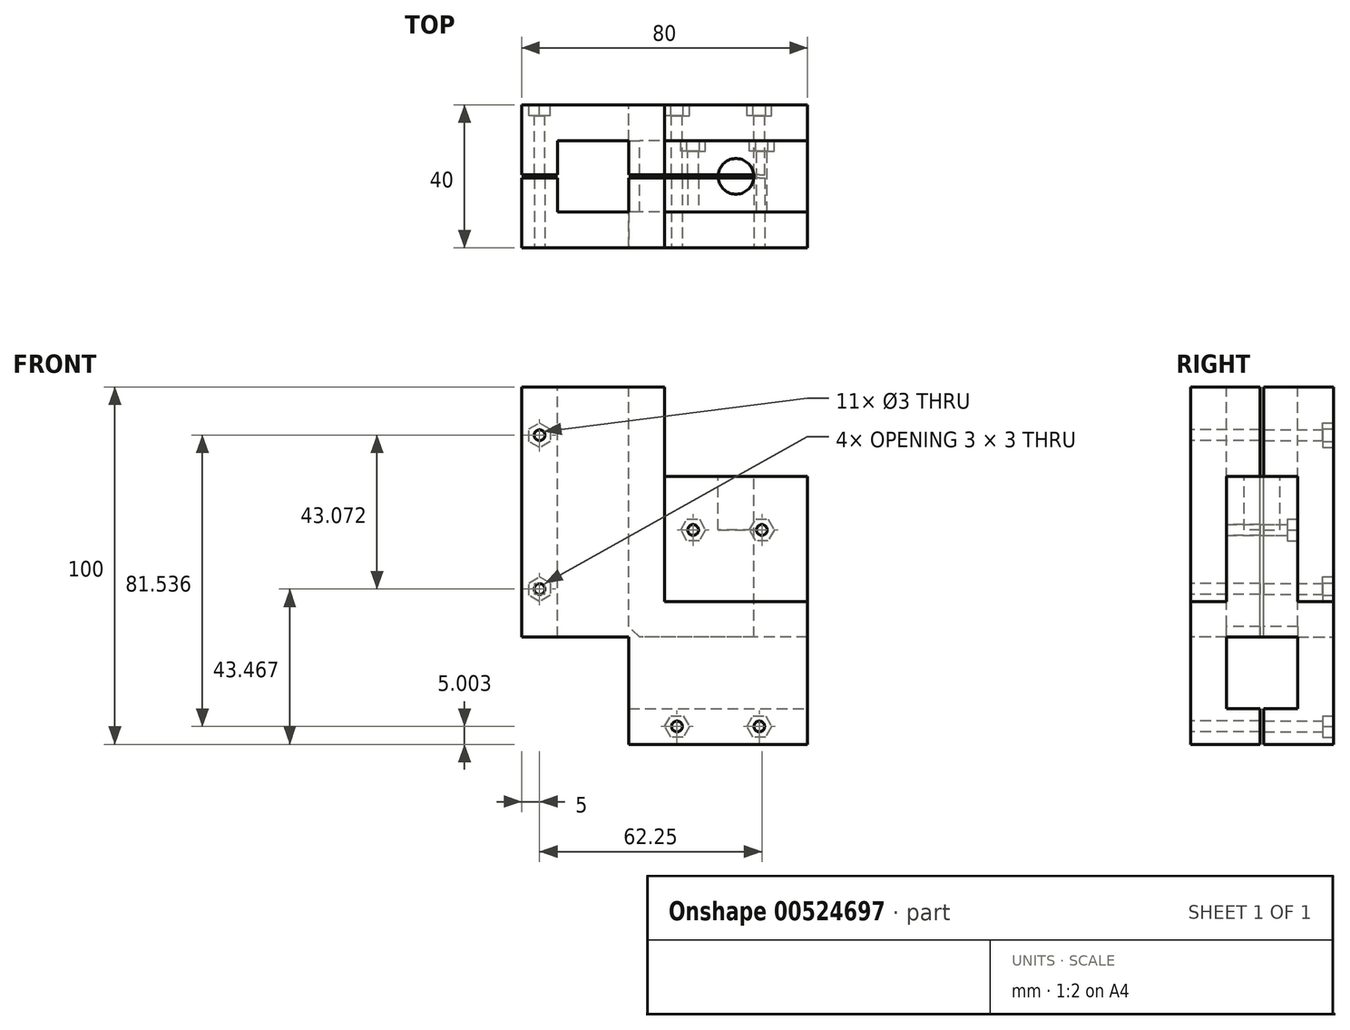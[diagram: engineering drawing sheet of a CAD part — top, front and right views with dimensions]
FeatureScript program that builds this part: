
annotation { "Feature Type Name" : "Feature", "Feature Type Description" : "" }
export const myFeature = defineFeature(function(context is Context, id is Id, definition is map)
    precondition{}
    {
        {
            var Q0;
            Q0=qCreatedBy(makeId("Front.planeOp"),FACE);
            var sketch = newSketch(context, id + "F0", { "sketchPlane" : qUnion([Q0])});
            skLineSegment(sketch, "E0", {"start": v(-50, 89.2) * mm, "end": v(-50, 19.2) * mm});
            skLineSegment(sketch, "E1", {"start": v(-50, 19.2) * mm, "end": v(0, 19.2) * mm});
            skLineSegment(sketch, "E2", {"start": v(0, 19.2) * mm, "end": v(0, 64.2) * mm});
            skLineSegment(sketch, "E3", {"start": v(0, 64.2) * mm, "end": v(-40, 64.2) * mm});
            skLineSegment(sketch, "E4", {"start": v(-40, 64.2) * mm, "end": v(-40, 89.2) * mm});
            skLineSegment(sketch, "E5", {"start": v(-40, 89.2) * mm, "end": v(-50, 89.2) * mm});
            skSolve(sketch);
        }
        {
            var Q0;
            Q0=qSketchRegion(id+"F0",true);
            extrude(context, id + "F1", {"entities" : qUnion([Q0]), "depth" : 20 * mm, "offsetDistance" : 25 * mm});
        }
        {
            var Q0;
            Q0=makeQuery(id+"F1.opExtrude","CAP_FACE",FACE,{"disambiguationData":[OSD([sQuery(id+"F0.wireOp",EDGE,"E0"),sQuery(id+"F0.wireOp",EDGE,"E1"),sQuery(id+"F0.wireOp",EDGE,"E2"),sQuery(id+"F0.wireOp",EDGE,"E3"),sQuery(id+"F0.wireOp",EDGE,"E4"),sQuery(id+"F0.wireOp",EDGE,"E5")])],"isStart":false});
            var sketch = newSketch(context, id + "F2", { "sketchPlane" : qUnion([Q0])});
            skLineSegment(sketch, "E6", {"start": v(-50, 29.2) * mm, "end": v(0, 29.2) * mm});
            skSolve(sketch);
        }
        {
            var Q0;
            {var subQ0=sQuery(id+"F2.wireOp",EDGE,"E6");Q0=makeQuery(id+"F2.imprint","IMPRINT",FACE,{"disambiguationData":[TD([[makeQuery(id+"F2.imprint","IMPRINT",EDGE,{"derivedFrom":subQ0}),-1.0]])]});}
            extrude(context, id + "F3", {"entities" : qUnion([Q0]), "operationType" : NewBodyOperationType.ADD, "depth" : 10 * mm, "offsetDistance" : 25 * mm});
        }
        {
            var Q0;
            Q0=makeQuery(id+"F1.opExtrude","CAP_FACE",FACE,{"disambiguationData":[OSD([sQuery(id+"F0.wireOp",EDGE,"E0"),sQuery(id+"F0.wireOp",EDGE,"E1"),sQuery(id+"F0.wireOp",EDGE,"E2"),sQuery(id+"F0.wireOp",EDGE,"E3"),sQuery(id+"F0.wireOp",EDGE,"E4"),sQuery(id+"F0.wireOp",EDGE,"E5")])],"isStart":true});
            var sketch = newSketch(context, id + "F4", { "sketchPlane" : qUnion([Q0])});
            skLineSegment(sketch, "E7", {"start": v(0, 29.2) * mm, "end": v(50, 29.2) * mm});
            skSolve(sketch);
        }
        {
            var Q0;
            {var subQ0=sQuery(id+"F4.wireOp",EDGE,"E7");Q0=makeQuery(id+"F4.imprint","IMPRINT",FACE,{"disambiguationData":[TD([[makeQuery(id+"F4.imprint","IMPRINT",EDGE,{"derivedFrom":subQ0}),-1.0]])]});}
            extrude(context, id + "F5", {"entities" : qUnion([Q0]), "operationType" : NewBodyOperationType.ADD, "depth" : 10 * mm, "offsetDistance" : 25 * mm});
        }
        {
            var Q0;
            {var subQ0=sQuery(id+"F0.wireOp",EDGE,"E1");Q0=makeQuery(id+"F5.boolean.opBoolean","MERGE",FACE,{"derivedFrom":[makeQuery(id+"F3.boolean.opBoolean","MERGE",FACE,{"derivedFrom":[makeQuery(id+"F1.opExtrude","SWEPT_FACE",FACE,{"disambiguationData":[OSD([subQ0])]}),makeQuery(id+"F3.opExtrude","SWEPT_FACE",FACE,{"disambiguationData":[OSD([subQ0])]})]}),makeQuery(id+"F5.opExtrude","SWEPT_FACE",FACE,{"disambiguationData":[OSD([subQ0])]})]});}
            var sketch = newSketch(context, id + "F6", { "sketchPlane" : qUnion([Q0])});
            skLineSegment(sketch, "E8", {"start": v(0, 20) * mm, "end": v(-50, 20) * mm});
            skLineSegment(sketch, "E9", {"start": v(0, 0) * mm, "end": v(-50, 0) * mm});
            skSolve(sketch);
        }
        {
            var Q0;
            {var subQ0=sQuery(id+"F6.wireOp",EDGE,"E8");Q0=makeQuery(id+"F6.imprint","IMPRINT",FACE,{"disambiguationData":[TD([[makeQuery(id+"F6.imprint","IMPRINT",EDGE,{"derivedFrom":subQ0}),-1.0]])]});}
            var Q1;
            {var subQ0=sQuery(id+"F6.wireOp",EDGE,"E9");Q1=makeQuery(id+"F6.imprint","IMPRINT",FACE,{"disambiguationData":[TD([[makeQuery(id+"F6.imprint","IMPRINT",EDGE,{"derivedFrom":subQ0}),1.0]])]});}
            extrude(context, id + "F7", {"entities" : qUnion([Q0, Q1]), "operationType" : NewBodyOperationType.ADD, "depth" : 30 * mm, "offsetDistance" : 25 * mm});
        }
        {
            var Q0;
            Q0=makeQuery(id+"F5.opExtrude","SWEPT_FACE",FACE,{"disambiguationData":[OSD([sQuery(id+"F4.wireOp",EDGE,"E7")])]});
            var sketch = newSketch(context, id + "F8", { "sketchPlane" : qUnion([Q0])});
            skLineSegment(sketch, "E10", {"start": v(-30, -25) * mm, "end": v(-28.27, -28) * mm});
            skLineSegment(sketch, "E11", {"start": v(-28.27, -28) * mm, "end": v(-24.8, -28) * mm});
            skLineSegment(sketch, "E12", {"start": v(-24.8, -28) * mm, "end": v(-23.07, -25) * mm});
            skLineSegment(sketch, "E13", {"start": v(-23.07, -25) * mm, "end": v(-24.8, -22) * mm});
            skLineSegment(sketch, "E14", {"start": v(-24.8, -22) * mm, "end": v(-28.27, -22) * mm});
            skLineSegment(sketch, "E15", {"start": v(-28.27, -22) * mm, "end": v(-30, -25) * mm});
            skCircle(sketch, "E16", {"center": v(-26.54, -25) * mm, "radius": 1.5 * mm});
            skLineSegment(sketch, "E17", {"start": v(-16.93, -25) * mm, "end": v(-15.2, -28) * mm});
            skLineSegment(sketch, "E18", {"start": v(-15.2, -28) * mm, "end": v(-11.73, -28) * mm});
            skLineSegment(sketch, "E19", {"start": v(-11.73, -28) * mm, "end": v(-10, -25) * mm});
            skLineSegment(sketch, "E20", {"start": v(-10, -25) * mm, "end": v(-11.73, -22) * mm});
            skLineSegment(sketch, "E21", {"start": v(-11.73, -22) * mm, "end": v(-15.2, -22) * mm});
            skLineSegment(sketch, "E22", {"start": v(-15.2, -22) * mm, "end": v(-16.93, -25) * mm});
            skCircle(sketch, "E23", {"center": v(-13.46, -25) * mm, "radius": 1.5 * mm});
            skLineSegment(sketch, "E24", {"start": v(-70, 5) * mm, "end": v(-68.27, 2) * mm});
            skLineSegment(sketch, "E25", {"start": v(-68.27, 2) * mm, "end": v(-64.8, 2) * mm});
            skLineSegment(sketch, "E26", {"start": v(-64.8, 2) * mm, "end": v(-63.07, 5) * mm});
            skLineSegment(sketch, "E27", {"start": v(-63.07, 5) * mm, "end": v(-64.8, 8) * mm});
            skLineSegment(sketch, "E28", {"start": v(-64.8, 8) * mm, "end": v(-68.27, 8) * mm});
            skLineSegment(sketch, "E29", {"start": v(-68.27, 8) * mm, "end": v(-70, 5) * mm});
            skCircle(sketch, "E30", {"center": v(-66.54, 5) * mm, "radius": 1.5 * mm});
            skLineSegment(sketch, "E31", {"start": v(-16.93, 5) * mm, "end": v(-15.2, 2) * mm});
            skLineSegment(sketch, "E32", {"start": v(-15.2, 2) * mm, "end": v(-11.73, 2) * mm});
            skLineSegment(sketch, "E33", {"start": v(-11.73, 2) * mm, "end": v(-10, 5) * mm});
            skLineSegment(sketch, "E34", {"start": v(-10, 5) * mm, "end": v(-11.73, 8) * mm});
            skLineSegment(sketch, "E35", {"start": v(-11.73, 8) * mm, "end": v(-15.2, 8) * mm});
            skLineSegment(sketch, "E36", {"start": v(-15.2, 8) * mm, "end": v(-16.93, 5) * mm});
            skCircle(sketch, "E37", {"center": v(-13.46, 5) * mm, "radius": 1.5 * mm});
            skLineSegment(sketch, "E38", {"start": v(-40, 0) * mm, "end": v(-40, 10) * mm});
            skLineSegment(sketch, "E39.bottom", {"start": v(-40, -20) * mm, "end": v(-50, -20) * mm});
            skLineSegment(sketch, "E39.top", {"start": v(-40, -30) * mm, "end": v(-50, -30) * mm});
            skLineSegment(sketch, "E39.left", {"start": v(-40, -20) * mm, "end": v(-40, -30) * mm});
            skLineSegment(sketch, "E39.right", {"start": v(-50, -20) * mm, "end": v(-50, -30) * mm});
            skSolve(sketch);
        }
        {
            var Q0;
            {var subQ0=sQuery(id+"F8.wireOp",EDGE,"E38");Q0=makeQuery(id+"F8.imprint","IMPRINT",FACE,{"disambiguationData":[TD([[makeQuery(id+"F8.imprint","IMPRINT",EDGE,{"derivedFrom":subQ0}),1.0]])]});}
            var Q1;
            Q1=makeQuery(id+"F8.imprint","IMPRINT",FACE,{"disambiguationData":[TD([[makeQuery(id+"F8.imprint","IMPRINT",EDGE,{"derivedFrom":sQuery(id+"F8.wireOp",EDGE,"E39.bottom")}),1.0]])]});
            extrude(context, id + "F9", {"entities" : qUnion([Q0, Q1]), "operationType" : NewBodyOperationType.ADD, "depth" : 60 * mm, "offsetDistance" : 25 * mm});
        }
        {
            var Q0;
            {var subQ0=sQuery(id+"F0.wireOp",EDGE,"E0");var subQ1=sQuery(id+"F0.wireOp",EDGE,"E1");var subQ2=makeQuery(id+"F5.boolean.opBoolean","MERGE",EDGE,{"derivedFrom":[makeQuery(id+"F3.boolean.opBoolean","MERGE",EDGE,{"derivedFrom":[makeQuery(id+"F1.opExtrude","SWEPT_EDGE",EDGE,{"disambiguationData":[OSD([subQ0,subQ1])]}),makeQuery(id+"F3.opExtrude","SWEPT_EDGE",EDGE,{"disambiguationData":[OSD([subQ0,subQ1])]})]}),makeQuery(id+"F5.opExtrude","SWEPT_EDGE",EDGE,{"disambiguationData":[OSD([subQ0,subQ1])]})]});Q0=makeQuery(id+"F9.boolean.opBoolean","MERGE",FACE,{"derivedFrom":[makeQuery(id+"F7.boolean.opBoolean","MERGE",FACE,{"derivedFrom":[makeQuery(id+"F5.boolean.opBoolean","MERGE",FACE,{"derivedFrom":[makeQuery(id+"F3.boolean.opBoolean","MERGE",FACE,{"derivedFrom":[makeQuery(id+"F1.opExtrude","SWEPT_FACE",FACE,{"disambiguationData":[OSD([subQ0])]}),makeQuery(id+"F3.opExtrude","SWEPT_FACE",FACE,{"disambiguationData":[OSD([subQ0])]})]}),makeQuery(id+"F5.opExtrude","SWEPT_FACE",FACE,{"disambiguationData":[OSD([subQ0])]})]}),makeQuery(id+"F7.opExtrude","SWEPT_FACE",FACE,{"disambiguationData":[OSD([subQ0,subQ1]),TDD([makeQuery(id+"F6.imprint","IMPRINT",EDGE,{"disambiguationData":[TD([[makeQuery(id+"F6.imprint","INTERSECT",VERTEX,{"derivedFrom":[makeQuery(id+"F3.opExtrude","CAP_EDGE",EDGE,{"disambiguationData":[OSD([subQ1])],"isStart":false}),subQ2]}),-1.0]])],"derivedFrom":subQ2})])]}),makeQuery(id+"F7.opExtrude","SWEPT_FACE",FACE,{"disambiguationData":[OSD([subQ0,subQ1]),TDD([makeQuery(id+"F6.imprint","IMPRINT",EDGE,{"disambiguationData":[TD([[makeQuery(id+"F6.imprint","INTERSECT",VERTEX,{"derivedFrom":[makeQuery(id+"F5.opExtrude","CAP_EDGE",EDGE,{"disambiguationData":[OSD([subQ1])],"isStart":false}),subQ2]}),1.0]])],"derivedFrom":subQ2})])]})]}),makeQuery(id+"F9.opExtrude","SWEPT_FACE",FACE,{"disambiguationData":[OSD([sQuery(id+"F8.wireOp",EDGE,"E39.right")])]}),makeQuery(id+"F9.opExtrude","SWEPT_FACE",FACE,{"disambiguationData":[OSD([subQ0,sQuery(id+"F4.wireOp",EDGE,"E7")])]})]});}
            var sketch = newSketch(context, id + "F10", { "sketchPlane" : qUnion([Q0])});
            skLineSegment(sketch, "E40", {"start": v(20, 19.2) * mm, "end": v(20, 89.2) * mm});
            skLineSegment(sketch, "E41", {"start": v(0, 19.2) * mm, "end": v(0, 89.2) * mm});
            skLineSegment(sketch, "E42", {"start": v(20, 19.2) * mm, "end": v(30, 19.2) * mm});
            skLineSegment(sketch, "E43", {"start": v(0, 19.2) * mm, "end": v(-10, 19.2) * mm});
            skSolve(sketch);
        }
        {
            var Q0;
            {var subQ0=sQuery(id+"F10.wireOp",EDGE,"E40");Q0=makeQuery(id+"F10.imprint","IMPRINT",FACE,{"disambiguationData":[TD([[makeQuery(id+"F10.imprint","IMPRINT",EDGE,{"derivedFrom":subQ0}),-1.0]])]});}
            var Q1;
            {var subQ0=sQuery(id+"F10.wireOp",EDGE,"E41");Q1=makeQuery(id+"F10.imprint","IMPRINT",FACE,{"disambiguationData":[TD([[makeQuery(id+"F10.imprint","IMPRINT",EDGE,{"derivedFrom":subQ0}),1.0]])]});}
            extrude(context, id + "F11", {"entities" : qUnion([Q0, Q1]), "operationType" : NewBodyOperationType.ADD, "depth" : 30 * mm, "offsetDistance" : 25 * mm});
        }
        {
            var Q0;
            Q0=makeQuery(id+"F1.opExtrude","SWEPT_FACE",FACE,{"disambiguationData":[OSD([sQuery(id+"F0.wireOp",EDGE,"E3")])]});
            var sketch = newSketch(context, id + "F12", { "sketchPlane" : qUnion([Q0])});
            skCircle(sketch, "E44", {"center": v(-20, -10) * mm, "radius": 5 * mm});
            skSolve(sketch);
        }
        {
            var Q0;
            Q0=makeQuery(id+"F12.imprint","IMPRINT",FACE,{"disambiguationData":[TD([[makeQuery(id+"F12.imprint","IMPRINT",EDGE,{"derivedFrom":sQuery(id+"F12.wireOp",EDGE,"E44")}),1.0]])]});
            extrude(context, id + "F13", {"entities" : qUnion([Q0]), "operationType" : NewBodyOperationType.REMOVE, "oppositeDirection" : true, "depth" : 15 * mm, "offsetDistance" : 25 * mm});
        }
        {
            var Q0;
            {var subQ0=sQuery(id+"F8.wireOp",EDGE,"E39.right");var subQ1=sQuery(id+"F8.wireOp",EDGE,"E39.top");var subQ3=sQuery(id+"F0.wireOp",EDGE,"E0");var subQ5=sQuery(id+"F4.wireOp",EDGE,"E7");var subQ6=sQuery(id+"F0.wireOp",EDGE,"E5");var subQ7=makeQuery(id+"F9.boolean.opBoolean","MERGE",EDGE,{"derivedFrom":[makeQuery(id+"F1.opExtrude","SWEPT_EDGE",EDGE,{"disambiguationData":[OSD([subQ3,subQ6])]}),makeQuery(id+"F9.opExtrude","CAP_EDGE",EDGE,{"disambiguationData":[OSD([subQ0])],"isStart":false}),makeQuery(id+"F9.opExtrude","CAP_EDGE",EDGE,{"disambiguationData":[OSD([subQ3,subQ5])],"isStart":false})]});Q0=makeQuery(id+"F11.boolean.opBoolean","MERGE",FACE,{"derivedFrom":[makeQuery(id+"F9.boolean.opBoolean","MERGE",FACE,{"derivedFrom":[makeQuery(id+"F1.opExtrude","SWEPT_FACE",FACE,{"disambiguationData":[OSD([subQ6])]}),makeQuery(id+"F9.opExtrude","CAP_FACE",FACE,{"disambiguationData":[OSD([subQ3,subQ5,sQuery(id+"F8.wireOp",EDGE,"E38")])],"isStart":false}),makeQuery(id+"F9.opExtrude","CAP_FACE",FACE,{"disambiguationData":[OSD([sQuery(id+"F8.wireOp",EDGE,"E39.bottom"),subQ1,sQuery(id+"F8.wireOp",EDGE,"E39.left"),subQ0])],"isStart":false})]}),makeQuery(id+"F11.opExtrude","SWEPT_FACE",FACE,{"disambiguationData":[OSD([subQ3,subQ6,subQ5,subQ0]),TDD([makeQuery(id+"F10.imprint","IMPRINT",EDGE,{"disambiguationData":[TD([[makeQuery(id+"F10.imprint","INTERSECT",VERTEX,{"derivedFrom":[subQ7,sQuery(id+"F10.wireOp",EDGE,"E41")]}),-1.0]])],"derivedFrom":subQ7})])]}),makeQuery(id+"F11.opExtrude","SWEPT_FACE",FACE,{"disambiguationData":[OSD([subQ3,subQ6,subQ5,subQ0]),TDD([makeQuery(id+"F10.imprint","IMPRINT",EDGE,{"disambiguationData":[TD([[makeQuery(id+"F10.imprint","INTERSECT",VERTEX,{"derivedFrom":[subQ7,sQuery(id+"F10.wireOp",EDGE,"E40")]}),1.0]])],"derivedFrom":subQ7})])]})]});}
            var sketch = newSketch(context, id + "F14", { "sketchPlane" : qUnion([Q0])});
            skLineSegment(sketch, "E45", {"start": v(-40, -10) * mm, "end": v(-40, -9.5) * mm});
            skLineSegment(sketch, "E46", {"start": v(-40, -10) * mm, "end": v(-40, -10.5) * mm});
            skLineSegment(sketch, "E47", {"start": v(-40, -10.5) * mm, "end": v(-50, -10.5) * mm});
            skLineSegment(sketch, "E48", {"start": v(-40, -9.5) * mm, "end": v(-50, -9.5) * mm});
            skSolve(sketch);
        }
        {
            var Q0;
            Q0=makeQuery(id+"F1.opExtrude","SWEPT_FACE",FACE,{"disambiguationData":[OSD([sQuery(id+"F0.wireOp",EDGE,"E3")])]});
            var sketch = newSketch(context, id + "F15", { "sketchPlane" : qUnion([Q0])});
            skLineSegment(sketch, "E49", {"start": v(-40, 54.2) * mm, "end": v(-40, -10.5) * mm});
            skLineSegment(sketch, "E50", {"start": v(-40, -10.5) * mm, "end": v(0, -10.5) * mm});
            skLineSegment(sketch, "E51", {"start": v(-40, -9.5) * mm, "end": v(0, -9.5) * mm});
            skSolve(sketch);
        }
        {
            var Q0;
            {var subQ0=sQuery(id+"F15.wireOp",EDGE,"E50");var subQ3=makeQuery(id+"F13.boolean.opBoolean","COPY",EDGE,{"derivedFrom":makeQuery(id+"F13.opExtrude","CAP_EDGE",EDGE,{"disambiguationData":[OSD([sQuery(id+"F12.wireOp",EDGE,"E44")])],"isStart":true})});var subQ4=makeQuery(id+"F15.imprint","INTERSECT",VERTEX,{"disambiguationData":[OD(1.0)],"derivedFrom":[subQ3,subQ0]});Q0=makeQuery(id+"F15.imprint","IMPRINT",FACE,{"disambiguationData":[TD([[makeQuery(id+"F15.imprint","IMPRINT",EDGE,{"disambiguationData":[TD([[subQ4,-1.0]])],"derivedFrom":subQ3}),-1.0]])]});}
            var Q1;
            Q1=makeQuery(id+"F14.imprint","IMPRINT",FACE,{"disambiguationData":[TD([[makeQuery(id+"F14.imprint","IMPRINT",EDGE,{"derivedFrom":sQuery(id+"F14.wireOp",EDGE,"E45")}),1.0]])]});
            var Q2;
            {var subQ0=sQuery(id+"F15.wireOp",EDGE,"E50");var subQ1=makeQuery(id+"F13.boolean.opBoolean","COPY",EDGE,{"derivedFrom":makeQuery(id+"F13.opExtrude","CAP_EDGE",EDGE,{"disambiguationData":[OSD([sQuery(id+"F12.wireOp",EDGE,"E44")])],"isStart":true})});var subQ2=makeQuery(id+"F15.imprint","INTERSECT",VERTEX,{"disambiguationData":[OD(0.0)],"derivedFrom":[subQ1,subQ0]});Q2=makeQuery(id+"F15.imprint","IMPRINT",FACE,{"disambiguationData":[TD([[makeQuery(id+"F15.imprint","IMPRINT",EDGE,{"disambiguationData":[TD([[subQ2,-1.0]])],"derivedFrom":subQ0}),1.0]])]});}
            var Q3;
            {var subQ1=sQuery(id+"F15.wireOp",EDGE,"E49");var subQ3=sQuery(id+"F15.wireOp",EDGE,"E51");var subQ4=makeQuery(id+"F15.imprint","INTERSECT",VERTEX,{"derivedFrom":[subQ1,subQ3]});Q3=makeQuery(id+"F15.imprint","IMPRINT",FACE,{"disambiguationData":[TD([[makeQuery(id+"F15.imprint","IMPRINT",EDGE,{"disambiguationData":[TD([[subQ4,-1.0]])],"derivedFrom":subQ3}),-1.0]])]});}
            extrude(context, id + "F16", {"entities" : qUnion([Q0, Q1, Q2, Q3]), "operationType" : NewBodyOperationType.REMOVE, "oppositeDirection" : true, "depth" : 70 * mm, "offsetDistance" : 25 * mm});
        }
        {
            var Q0;
            {var subQ0=sQuery(id+"F0.wireOp",EDGE,"E1");var subQ1=sQuery(id+"F0.wireOp",EDGE,"E0");var subQ2=makeQuery(id+"F5.boolean.opBoolean","MERGE",EDGE,{"derivedFrom":[makeQuery(id+"F3.boolean.opBoolean","MERGE",EDGE,{"derivedFrom":[makeQuery(id+"F1.opExtrude","SWEPT_EDGE",EDGE,{"disambiguationData":[OSD([subQ1,subQ0])]}),makeQuery(id+"F3.opExtrude","SWEPT_EDGE",EDGE,{"disambiguationData":[OSD([subQ1,subQ0])]})]}),makeQuery(id+"F5.opExtrude","SWEPT_EDGE",EDGE,{"disambiguationData":[OSD([subQ1,subQ0])]})]});var subQ3=sQuery(id+"F6.wireOp",EDGE,"E9");Q0=makeQuery(id+"F16.boolean.opBoolean","SPLIT",EDGE,{"disambiguationData":[TD([makeQuery(id+"F7.opExtrude","SWEPT_FACE",FACE,{"disambiguationData":[OSD([subQ3])]})])],"derivedFrom":subQ2});}
            var Q1;
            {var subQ0=sQuery(id+"F0.wireOp",EDGE,"E1");var subQ1=sQuery(id+"F0.wireOp",EDGE,"E0");var subQ2=makeQuery(id+"F5.boolean.opBoolean","MERGE",EDGE,{"derivedFrom":[makeQuery(id+"F3.boolean.opBoolean","MERGE",EDGE,{"derivedFrom":[makeQuery(id+"F1.opExtrude","SWEPT_EDGE",EDGE,{"disambiguationData":[OSD([subQ1,subQ0])]}),makeQuery(id+"F3.opExtrude","SWEPT_EDGE",EDGE,{"disambiguationData":[OSD([subQ1,subQ0])]})]}),makeQuery(id+"F5.opExtrude","SWEPT_EDGE",EDGE,{"disambiguationData":[OSD([subQ1,subQ0])]})]});var subQ3=sQuery(id+"F6.wireOp",EDGE,"E8");Q1=makeQuery(id+"F16.boolean.opBoolean","SPLIT",EDGE,{"disambiguationData":[TD([makeQuery(id+"F7.opExtrude","SWEPT_FACE",FACE,{"disambiguationData":[OSD([subQ3])]})])],"derivedFrom":subQ2});}
            chamfer(context, id + "F17", {"entities" : qUnion([Q0, Q1]), "width" : 3 * mm, "tangentPropagation" : true});
        }
        {
            var Q0;
            Q0=makeQuery(id+"F17.opChamfer","MERGE",FACE,{"derivedFrom":[makeQuery(id+"F7.opExtrude","SWEPT_FACE",FACE,{"disambiguationData":[OSD([sQuery(id+"F6.wireOp",EDGE,"E9")])]}),makeQuery(id+"F11.opExtrude","SWEPT_FACE",FACE,{"disambiguationData":[OSD([sQuery(id+"F10.wireOp",EDGE,"E41")])]})]});
            var sketch = newSketch(context, id + "F18", { "sketchPlane" : qUnion([Q0])});
            skLineSegment(sketch, "E52", {"start": v(-80, 19.2) * mm, "end": v(-70, 19.2) * mm});
            skLineSegment(sketch, "E53", {"start": v(-70, 19.2) * mm, "end": v(-70, 89.2) * mm});
            skLineSegment(sketch, "E54", {"start": v(-50, -10.8) * mm, "end": v(-50, -0.8) * mm});
            skLineSegment(sketch, "E55", {"start": v(-50, -0.8) * mm, "end": v(0, -0.8) * mm});
            skSolve(sketch);
        }
        {
            var Q0;
            Q0=makeQuery(id+"F17.opChamfer","MERGE",FACE,{"derivedFrom":[makeQuery(id+"F7.opExtrude","SWEPT_FACE",FACE,{"disambiguationData":[OSD([sQuery(id+"F6.wireOp",EDGE,"E8")])]}),makeQuery(id+"F11.opExtrude","SWEPT_FACE",FACE,{"disambiguationData":[OSD([sQuery(id+"F10.wireOp",EDGE,"E40")])]})]});
            var sketch = newSketch(context, id + "F19", { "sketchPlane" : qUnion([Q0])});
            skLineSegment(sketch, "E56", {"start": v(80, 19.2) * mm, "end": v(70, 19.2) * mm});
            skLineSegment(sketch, "E57", {"start": v(70, 19.2) * mm, "end": v(70, 89.2) * mm});
            skLineSegment(sketch, "E58", {"start": v(50, -10.8) * mm, "end": v(50, -0.8) * mm});
            skLineSegment(sketch, "E59", {"start": v(50, -0.8) * mm, "end": v(0, -0.8) * mm});
            skSolve(sketch);
        }
        {
            var Q0;
            Q0=makeQuery(id+"F18.imprint","IMPRINT",FACE,{"disambiguationData":[TD([[makeQuery(id+"F18.imprint","IMPRINT",EDGE,{"derivedFrom":sQuery(id+"F18.wireOp",EDGE,"E52")}),1.0]])]});
            var Q1;
            Q1=makeQuery(id+"F18.imprint","IMPRINT",FACE,{"disambiguationData":[TD([[makeQuery(id+"F18.imprint","IMPRINT",EDGE,{"derivedFrom":sQuery(id+"F18.wireOp",EDGE,"E54")}),-1.0]])]});
            extrude(context, id + "F20", {"entities" : qUnion([Q0, Q1]), "operationType" : NewBodyOperationType.ADD, "depth" : 9.5 * mm, "offsetDistance" : 25 * mm});
        }
        {
            var Q0;
            Q0=makeQuery(id+"F19.imprint","IMPRINT",FACE,{"disambiguationData":[TD([[makeQuery(id+"F19.imprint","IMPRINT",EDGE,{"derivedFrom":sQuery(id+"F19.wireOp",EDGE,"E56")}),-1.0]])]});
            var Q1;
            Q1=makeQuery(id+"F19.imprint","IMPRINT",FACE,{"disambiguationData":[TD([[makeQuery(id+"F19.imprint","IMPRINT",EDGE,{"derivedFrom":sQuery(id+"F19.wireOp",EDGE,"E58")}),1.0]])]});
            extrude(context, id + "F21", {"entities" : qUnion([Q0, Q1]), "operationType" : NewBodyOperationType.ADD, "depth" : 9.5 * mm, "offsetDistance" : 25 * mm});
        }
        {
            var Q0;
            {var subQ0=sQuery(id+"F8.wireOp",EDGE,"E39.top");var subQ1=sQuery(id+"F0.wireOp",EDGE,"E1");var subQ2=sQuery(id+"F0.wireOp",EDGE,"E0");Q0=makeQuery(id+"F11.boolean.opBoolean","MERGE",FACE,{"derivedFrom":[makeQuery(id+"F9.boolean.opBoolean","MERGE",FACE,{"derivedFrom":[makeQuery(id+"F7.boolean.opBoolean","MERGE",FACE,{"derivedFrom":[makeQuery(id+"F3.opExtrude","CAP_FACE",FACE,{"disambiguationData":[OSD([subQ2,subQ1,sQuery(id+"F0.wireOp",EDGE,"E2"),sQuery(id+"F2.wireOp",EDGE,"E6")])],"isStart":false}),makeQuery(id+"F7.opExtrude","SWEPT_FACE",FACE,{"disambiguationData":[OSD([subQ1]),TDD([makeQuery(id+"F6.imprint","IMPRINT",EDGE,{"derivedFrom":makeQuery(id+"F3.opExtrude","CAP_EDGE",EDGE,{"disambiguationData":[OSD([subQ1])],"isStart":false})})])]})]}),makeQuery(id+"F9.opExtrude","SWEPT_FACE",FACE,{"disambiguationData":[OSD([subQ0])]})]}),makeQuery(id+"F11.opExtrude","SWEPT_FACE",FACE,{"disambiguationData":[OSD([subQ2,subQ1,subQ0,sQuery(id+"F8.wireOp",EDGE,"E39.right")])]})]});}
            var sketch = newSketch(context, id + "F22", { "sketchPlane" : qUnion([Q0])});
            skCircle(sketch, "E60", {"center": v(-13.46, -5.8) * mm, "radius": 1.5 * mm});
            skCircle(sketch, "E61", {"center": v(-36.54, -5.8) * mm, "radius": 1.5 * mm});
            skCircle(sketch, "E62", {"center": v(-75, 75.73) * mm, "radius": 1.5 * mm});
            skCircle(sketch, "E63", {"center": v(-75, 32.66) * mm, "radius": 1.5 * mm});
            skSolve(sketch);
        }
        {
            var Q0;
            Q0=makeQuery(id+"F22.imprint","IMPRINT",FACE,{"disambiguationData":[TD([[makeQuery(id+"F22.imprint","IMPRINT",EDGE,{"derivedFrom":sQuery(id+"F22.wireOp",EDGE,"E60")}),1.0]])]});
            var Q1;
            Q1=makeQuery(id+"F22.imprint","IMPRINT",FACE,{"disambiguationData":[TD([[makeQuery(id+"F22.imprint","IMPRINT",EDGE,{"derivedFrom":sQuery(id+"F22.wireOp",EDGE,"E62")}),1.0]])]});
            var Q2;
            Q2=makeQuery(id+"F22.imprint","IMPRINT",FACE,{"disambiguationData":[TD([[makeQuery(id+"F22.imprint","IMPRINT",EDGE,{"derivedFrom":sQuery(id+"F22.wireOp",EDGE,"E63")}),1.0]])]});
            var Q3;
            Q3=makeQuery(id+"F22.imprint","IMPRINT",FACE,{"disambiguationData":[TD([[makeQuery(id+"F22.imprint","IMPRINT",EDGE,{"derivedFrom":sQuery(id+"F22.wireOp",EDGE,"E61")}),1.0]])]});
            extrude(context, id + "F23", {"entities" : qUnion([Q0, Q1, Q2, Q3]), "operationType" : NewBodyOperationType.REMOVE, "oppositeDirection" : true, "depth" : 20 * mm, "offsetDistance" : 25 * mm});
        }
        {
            var Q0;
            {var subQ0=sQuery(id+"F4.wireOp",EDGE,"E7");var subQ1=sQuery(id+"F0.wireOp",EDGE,"E1");var subQ2=sQuery(id+"F0.wireOp",EDGE,"E0");var subQ3=makeQuery(id+"F5.opExtrude","CAP_EDGE",EDGE,{"disambiguationData":[OSD([subQ0])],"isStart":false});Q0=makeQuery(id+"F11.boolean.opBoolean","MERGE",FACE,{"derivedFrom":[makeQuery(id+"F9.boolean.opBoolean","MERGE",FACE,{"derivedFrom":[makeQuery(id+"F7.boolean.opBoolean","MERGE",FACE,{"derivedFrom":[makeQuery(id+"F5.opExtrude","CAP_FACE",FACE,{"disambiguationData":[OSD([subQ2,subQ1,sQuery(id+"F0.wireOp",EDGE,"E2"),subQ0])],"isStart":false}),makeQuery(id+"F7.opExtrude","SWEPT_FACE",FACE,{"disambiguationData":[OSD([subQ1]),TDD([makeQuery(id+"F6.imprint","IMPRINT",EDGE,{"derivedFrom":makeQuery(id+"F5.opExtrude","CAP_EDGE",EDGE,{"disambiguationData":[OSD([subQ1])],"isStart":false})})])]})]}),makeQuery(id+"F9.opExtrude","SWEPT_FACE",FACE,{"disambiguationData":[OSD([subQ0]),TDD([makeQuery(id+"F8.imprint","IMPRINT",EDGE,{"disambiguationData":[TD([[makeQuery(id+"F8.imprint","INTERSECT",VERTEX,{"derivedFrom":[subQ3,sQuery(id+"F8.wireOp",EDGE,"E38")]}),-1.0]])],"derivedFrom":subQ3})])]})]}),makeQuery(id+"F11.opExtrude","SWEPT_FACE",FACE,{"disambiguationData":[OSD([subQ2,subQ1,subQ0])]})]});}
            var sketch = newSketch(context, id + "F24", { "sketchPlane" : qUnion([Q0])});
            skLineSegment(sketch, "E64", {"start": v(10, -5.8) * mm, "end": v(11.73, -8.8) * mm});
            skLineSegment(sketch, "E65", {"start": v(11.73, -8.8) * mm, "end": v(15.2, -8.8) * mm});
            skLineSegment(sketch, "E66", {"start": v(15.2, -8.8) * mm, "end": v(16.93, -5.8) * mm});
            skLineSegment(sketch, "E67", {"start": v(16.93, -5.8) * mm, "end": v(15.2, -2.8) * mm});
            skLineSegment(sketch, "E68", {"start": v(15.2, -2.8) * mm, "end": v(11.73, -2.8) * mm});
            skLineSegment(sketch, "E69", {"start": v(11.73, -2.8) * mm, "end": v(10, -5.8) * mm});
            skCircle(sketch, "E70", {"center": v(13.46, -5.8) * mm, "radius": 1.5 * mm});
            skLineSegment(sketch, "E71", {"start": v(33.07, -5.8) * mm, "end": v(34.8, -8.8) * mm});
            skLineSegment(sketch, "E72", {"start": v(34.8, -8.8) * mm, "end": v(38.27, -8.8) * mm});
            skLineSegment(sketch, "E73", {"start": v(38.27, -8.8) * mm, "end": v(40, -5.8) * mm});
            skLineSegment(sketch, "E74", {"start": v(40, -5.8) * mm, "end": v(38.27, -2.8) * mm});
            skLineSegment(sketch, "E75", {"start": v(38.27, -2.8) * mm, "end": v(34.8, -2.8) * mm});
            skLineSegment(sketch, "E76", {"start": v(34.8, -2.8) * mm, "end": v(33.07, -5.8) * mm});
            skCircle(sketch, "E77", {"center": v(36.54, -5.8) * mm, "radius": 1.5 * mm});
            skLineSegment(sketch, "E78", {"start": v(75, 29.2) * mm, "end": v(78, 30.93) * mm});
            skLineSegment(sketch, "E79", {"start": v(78, 30.93) * mm, "end": v(78, 34.39) * mm});
            skLineSegment(sketch, "E80", {"start": v(78, 34.39) * mm, "end": v(75, 36.12) * mm});
            skLineSegment(sketch, "E81", {"start": v(75, 36.12) * mm, "end": v(72, 34.39) * mm});
            skLineSegment(sketch, "E82", {"start": v(72, 34.39) * mm, "end": v(72, 30.93) * mm});
            skLineSegment(sketch, "E83", {"start": v(72, 30.93) * mm, "end": v(75, 29.2) * mm});
            skCircle(sketch, "E84", {"center": v(75, 32.66) * mm, "radius": 1.5 * mm});
            skLineSegment(sketch, "E85", {"start": v(75, 72.26) * mm, "end": v(78, 74) * mm});
            skLineSegment(sketch, "E86", {"start": v(78, 74) * mm, "end": v(78, 77.46) * mm});
            skLineSegment(sketch, "E87", {"start": v(78, 77.46) * mm, "end": v(75, 79.2) * mm});
            skLineSegment(sketch, "E88", {"start": v(75, 79.2) * mm, "end": v(72, 77.46) * mm});
            skLineSegment(sketch, "E89", {"start": v(72, 77.46) * mm, "end": v(72, 74) * mm});
            skLineSegment(sketch, "E90", {"start": v(72, 74) * mm, "end": v(75, 72.26) * mm});
            skCircle(sketch, "E91", {"center": v(75, 75.73) * mm, "radius": 1.5 * mm});
            skSolve(sketch);
        }
        {
            var Q0;
            Q0=makeQuery(id+"F24.imprint","IMPRINT",FACE,{"disambiguationData":[TD([[makeQuery(id+"F24.imprint","IMPRINT",EDGE,{"derivedFrom":sQuery(id+"F24.wireOp",EDGE,"E70")}),1.0]])]});
            var Q1;
            Q1=makeQuery(id+"F24.imprint","IMPRINT",FACE,{"disambiguationData":[TD([[makeQuery(id+"F24.imprint","IMPRINT",EDGE,{"derivedFrom":sQuery(id+"F24.wireOp",EDGE,"E77")}),1.0]])]});
            var Q2;
            Q2=makeQuery(id+"F24.imprint","IMPRINT",FACE,{"disambiguationData":[TD([[makeQuery(id+"F24.imprint","IMPRINT",EDGE,{"derivedFrom":sQuery(id+"F24.wireOp",EDGE,"E84")}),1.0]])]});
            var Q3;
            Q3=makeQuery(id+"F24.imprint","IMPRINT",FACE,{"disambiguationData":[TD([[makeQuery(id+"F24.imprint","IMPRINT",EDGE,{"derivedFrom":sQuery(id+"F24.wireOp",EDGE,"E91")}),1.0]])]});
            extrude(context, id + "F25", {"entities" : qUnion([Q0, Q1, Q2, Q3]), "operationType" : NewBodyOperationType.REMOVE, "oppositeDirection" : true, "depth" : 20 * mm, "offsetDistance" : 25 * mm});
        }
        {
            var Q0;
            Q0=makeQuery(id+"F24.imprint","IMPRINT",FACE,{"disambiguationData":[TD([[makeQuery(id+"F24.imprint","IMPRINT",EDGE,{"derivedFrom":sQuery(id+"F24.wireOp",EDGE,"E71")}),1.0]])]});
            var Q1;
            Q1=makeQuery(id+"F24.imprint","IMPRINT",FACE,{"disambiguationData":[TD([[makeQuery(id+"F24.imprint","IMPRINT",EDGE,{"derivedFrom":sQuery(id+"F24.wireOp",EDGE,"E64")}),1.0]])]});
            var Q2;
            Q2=makeQuery(id+"F24.imprint","IMPRINT",FACE,{"disambiguationData":[TD([[makeQuery(id+"F24.imprint","IMPRINT",EDGE,{"derivedFrom":sQuery(id+"F24.wireOp",EDGE,"E78")}),1.0]])]});
            var Q3;
            Q3=makeQuery(id+"F24.imprint","IMPRINT",FACE,{"disambiguationData":[TD([[makeQuery(id+"F24.imprint","IMPRINT",EDGE,{"derivedFrom":sQuery(id+"F24.wireOp",EDGE,"E85")}),1.0]])]});
            extrude(context, id + "F26", {"entities" : qUnion([Q0, Q1, Q2, Q3]), "operationType" : NewBodyOperationType.REMOVE, "depth" : -3 * mm, "offsetDistance" : 25 * mm});
        }
        {
            var Q0;
            Q0=makeQuery(id+"F1.opExtrude","CAP_FACE",FACE,{"disambiguationData":[OSD([sQuery(id+"F0.wireOp",EDGE,"E0"),sQuery(id+"F0.wireOp",EDGE,"E1"),sQuery(id+"F0.wireOp",EDGE,"E2"),sQuery(id+"F0.wireOp",EDGE,"E3"),sQuery(id+"F0.wireOp",EDGE,"E4"),sQuery(id+"F0.wireOp",EDGE,"E5")])],"isStart":false});
            var sketch = newSketch(context, id + "F27", { "sketchPlane" : qUnion([Q0])});
            skCircle(sketch, "E92", {"center": v(-32, 49.2) * mm, "radius": 1.5 * mm});
            skCircle(sketch, "E93", {"center": v(-12.75, 49.2) * mm, "radius": 1.5 * mm});
            skSolve(sketch);
        }
        {
            var Q0;
            Q0=makeQuery(id+"F1.opExtrude","CAP_FACE",FACE,{"disambiguationData":[OSD([sQuery(id+"F0.wireOp",EDGE,"E0"),sQuery(id+"F0.wireOp",EDGE,"E1"),sQuery(id+"F0.wireOp",EDGE,"E2"),sQuery(id+"F0.wireOp",EDGE,"E3"),sQuery(id+"F0.wireOp",EDGE,"E4"),sQuery(id+"F0.wireOp",EDGE,"E5")])],"isStart":true});
            var sketch = newSketch(context, id + "F28", { "sketchPlane" : qUnion([Q0])});
            skLineSegment(sketch, "E94", {"start": v(9.29, 49.2) * mm, "end": v(11.02, 46.2) * mm});
            skLineSegment(sketch, "E95", {"start": v(11.02, 46.2) * mm, "end": v(14.48, 46.2) * mm});
            skLineSegment(sketch, "E96", {"start": v(14.48, 46.2) * mm, "end": v(16.21, 49.2) * mm});
            skLineSegment(sketch, "E97", {"start": v(16.21, 49.2) * mm, "end": v(14.48, 52.2) * mm});
            skLineSegment(sketch, "E98", {"start": v(14.48, 52.2) * mm, "end": v(11.02, 52.2) * mm});
            skLineSegment(sketch, "E99", {"start": v(11.02, 52.2) * mm, "end": v(9.29, 49.2) * mm});
            skCircle(sketch, "E100", {"center": v(12.75, 49.2) * mm, "radius": 1.5 * mm});
            skLineSegment(sketch, "E101", {"start": v(28.54, 49.2) * mm, "end": v(30.27, 46.2) * mm});
            skLineSegment(sketch, "E102", {"start": v(30.27, 46.2) * mm, "end": v(33.73, 46.2) * mm});
            skLineSegment(sketch, "E103", {"start": v(33.73, 46.2) * mm, "end": v(35.46, 49.2) * mm});
            skLineSegment(sketch, "E104", {"start": v(35.46, 49.2) * mm, "end": v(33.73, 52.2) * mm});
            skLineSegment(sketch, "E105", {"start": v(33.73, 52.2) * mm, "end": v(30.27, 52.2) * mm});
            skLineSegment(sketch, "E106", {"start": v(30.27, 52.2) * mm, "end": v(28.54, 49.2) * mm});
            skCircle(sketch, "E107", {"center": v(32, 49.2) * mm, "radius": 1.5 * mm});
            skSolve(sketch);
        }
        {
            var Q0;
            Q0=makeQuery(id+"F28.imprint","IMPRINT",FACE,{"disambiguationData":[TD([[makeQuery(id+"F28.imprint","IMPRINT",EDGE,{"derivedFrom":sQuery(id+"F28.wireOp",EDGE,"E107")}),1.0]])]});
            var Q1;
            Q1=makeQuery(id+"F28.imprint","IMPRINT",FACE,{"disambiguationData":[TD([[makeQuery(id+"F28.imprint","IMPRINT",EDGE,{"derivedFrom":sQuery(id+"F28.wireOp",EDGE,"E100")}),1.0]])]});
            extrude(context, id + "F29", {"entities" : qUnion([Q0, Q1]), "operationType" : NewBodyOperationType.REMOVE, "oppositeDirection" : true, "depth" : 10 * mm, "offsetDistance" : 25 * mm});
        }
        {
            var Q0;
            Q0=makeQuery(id+"F27.imprint","IMPRINT",FACE,{"disambiguationData":[TD([[makeQuery(id+"F27.imprint","IMPRINT",EDGE,{"derivedFrom":sQuery(id+"F27.wireOp",EDGE,"E92")}),1.0]])]});
            var Q1;
            Q1=makeQuery(id+"F27.imprint","IMPRINT",FACE,{"disambiguationData":[TD([[makeQuery(id+"F27.imprint","IMPRINT",EDGE,{"derivedFrom":sQuery(id+"F27.wireOp",EDGE,"E93")}),1.0]])]});
            extrude(context, id + "F30", {"entities" : qUnion([Q0, Q1]), "operationType" : NewBodyOperationType.REMOVE, "oppositeDirection" : true, "depth" : 10 * mm, "offsetDistance" : 25 * mm});
        }
        {
            var Q0;
            Q0=makeQuery(id+"F28.imprint","IMPRINT",FACE,{"disambiguationData":[TD([[makeQuery(id+"F28.imprint","IMPRINT",EDGE,{"derivedFrom":sQuery(id+"F28.wireOp",EDGE,"E101")}),1.0]])]});
            var Q1;
            Q1=makeQuery(id+"F28.imprint","IMPRINT",FACE,{"disambiguationData":[TD([[makeQuery(id+"F28.imprint","IMPRINT",EDGE,{"derivedFrom":sQuery(id+"F28.wireOp",EDGE,"E94")}),1.0]])]});
            extrude(context, id + "F31", {"entities" : qUnion([Q0, Q1]), "operationType" : NewBodyOperationType.REMOVE, "oppositeDirection" : true, "depth" : 3 * mm, "offsetDistance" : 25 * mm});
        }
    });
